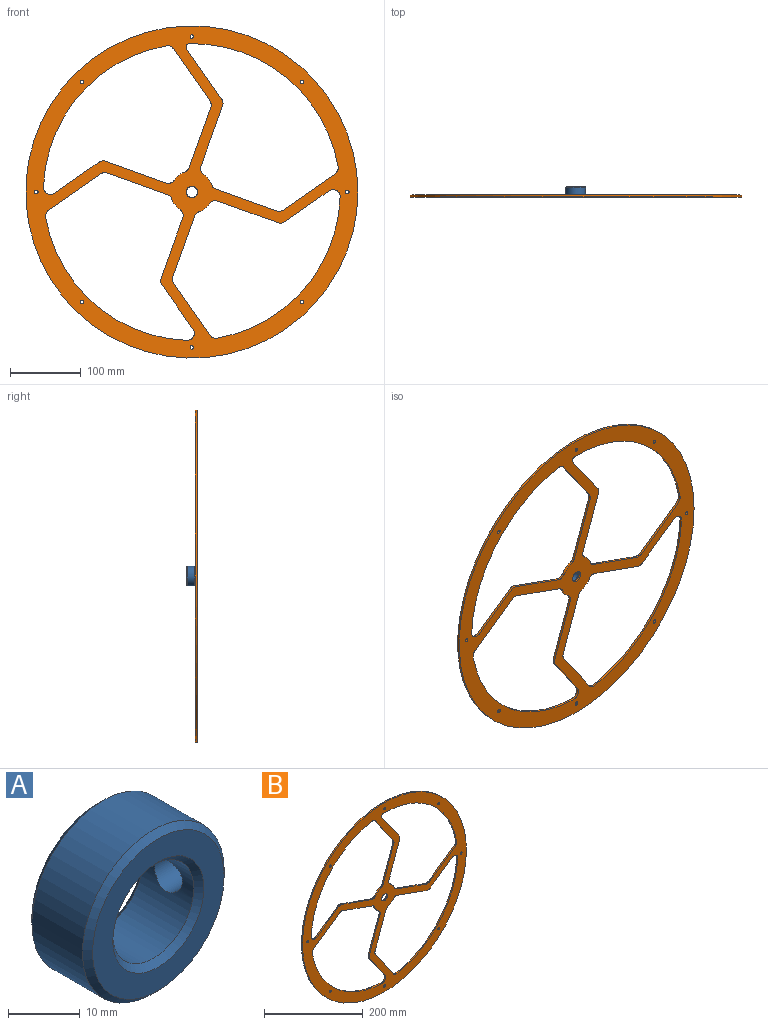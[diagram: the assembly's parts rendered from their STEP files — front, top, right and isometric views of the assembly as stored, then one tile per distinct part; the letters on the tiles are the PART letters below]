
ASSEMBLY  parts=2 mates=1
PART A: 9 faces, bbox 28x12x28 mm
  f0: cylinder r=8mm len=16mm, axis (0,1,0), area 478.6mm2, adj f4,f5,f8
  f1: cylinder r=14mm len=28mm, axis (0,1,0), area 855.9mm2, adj f6,f7,f8
  f2: plane 26x26mm, normal (0,-1,0), area 276.5mm2, adj f4,f6
  f3: plane 26x26mm, normal (0,1,0), area 276.5mm2, adj f5,f7
  f4: cone r=8mm half-angle=45deg, axis (0,-1,0), area 75.5mm2, adj f0,f2
  f5: cone r=9mm half-angle=45deg, axis (0,1,0), area 75.5mm2, adj f0,f3
  f6: cone r=13mm half-angle=45deg, axis (0,1,0), area 120mm2, adj f1,f2
  f7: cone r=14mm half-angle=45deg, axis (0,-1,0), area 120mm2, adj f1,f3
  f8: cylinder r=2.75mm len=6.49mm, axis (1,0,0), area 105.5mm2, adj f0,f1
PART B: 60 faces, bbox 470x3x470 mm
  f0: cylinder r=10mm len=9.9mm, axis (0,1,0), area 34mm2, adj f1,f44,f58,f59
  f1: plane 73.72x51.62mm, normal (0.82,0,0.57), area 270mm2, adj f0,f2,f58,f59
  f2: cylinder r=10mm len=9.11mm, axis (0,1,0), area 28.7mm2, adj f1,f3,f58,f59
  f3: plane 85.6x30.7mm, normal (0.94,0,-0.34), area 272.8mm2, adj f2,f4,f58,f59
  f4: cylinder r=10mm len=6.09mm, axis (0,1,0), area 26.6mm2, adj f3,f5,f58,f59
  f5: cylinder r=30mm len=14.95mm, axis (0,1,0), area 57.7mm2, adj f4,f6,f58,f59
  f6: cylinder r=10mm len=11.68mm, axis (0,1,0), area 39.7mm2, adj f5,f7,f58,f59
  f7: plane 85.6x30.7mm, normal (-0.34,0,-0.94), area 272.8mm2, adj f6,f8,f58,f59
  f8: cylinder r=10mm len=9.11mm, axis (0,1,0), area 28.7mm2, adj f7,f9,f58,f59
  f9: plane 62.85x44.01mm, normal (0.57,0,-0.82), area 230.2mm2, adj f8,f10,f58,f59
  f10: cylinder r=10mm len=15.74mm, axis (0,1,0), area 66.4mm2, adj f9,f44,f58,f59
  f11: cylinder r=10mm len=6.09mm, axis (0,1,0), area 26.6mm2, adj f12,f45,f58,f59
  f12: cylinder r=30mm len=14.95mm, axis (0,1,0), area 57.7mm2, adj f11,f13,f58,f59
  f13: cylinder r=10mm len=11.68mm, axis (0,1,0), area 39.7mm2, adj f12,f14,f58,f59
  f14: plane 85.6x30.7mm, normal (0.94,0,-0.34), area 272.8mm2, adj f13,f15,f58,f59
  f15: cylinder r=10mm len=9.11mm, axis (0,1,0), area 28.7mm2, adj f14,f16,f58,f59
  f16: plane 70.8x49.57mm, normal (0.82,0,0.57), area 259.3mm2, adj f15,f17,f58,f59
  f17: cylinder r=5mm len=7.87mm, axis (0,1,0), area 32.5mm2, adj f16,f18,f58,f59
  f18: cylinder r=210mm len=210.12mm, axis (0,1,0), area 890.9mm2, adj f17,f19,f58,f59
  f19: cylinder r=10mm len=9.9mm, axis (0,1,0), area 34mm2, adj f18,f20,f58,f59
  f20: plane 73.72x51.62mm, normal (-0.57,0,0.82), area 270mm2, adj f19,f21,f58,f59
  f21: cylinder r=10mm len=9.11mm, axis (0,1,0), area 28.7mm2, adj f20,f45,f58,f59
  f22: cylinder r=10mm len=9.11mm, axis (0,1,0), area 28.7mm2, adj f23,f46,f58,f59
  f23: plane 62.85x44.01mm, normal (-0.57,0,0.82), area 230.2mm2, adj f22,f24,f58,f59
  f24: cylinder r=10mm len=15.74mm, axis (0,1,0), area 66.4mm2, adj f23,f25,f58,f59
  f25: cylinder r=210mm len=200.05mm, axis (0,1,0), area 860.7mm2, adj f24,f26,f58,f59
  f26: cylinder r=10mm len=9.9mm, axis (0,1,0), area 34mm2, adj f25,f27,f58,f59
  f27: plane 73.72x51.62mm, normal (-0.82,0,-0.57), area 270mm2, adj f26,f28,f58,f59
  f28: cylinder r=10mm len=9.11mm, axis (0,1,0), area 28.7mm2, adj f27,f29,f58,f59
  f29: plane 85.6x30.7mm, normal (-0.94,0,0.34), area 272.8mm2, adj f28,f30,f58,f59
  f30: cylinder r=10mm len=6.09mm, axis (0,1,0), area 26.6mm2, adj f29,f31,f58,f59
  f31: cylinder r=30mm len=14.95mm, axis (0,1,0), area 57.7mm2, adj f30,f32,f58,f59
  f32: cylinder r=10mm len=11.68mm, axis (0,1,0), area 39.7mm2, adj f31,f46,f58,f59
  f33: cylinder r=10mm len=11.68mm, axis (0,1,0), area 39.7mm2, adj f34,f47,f58,f59
  f34: plane 85.6x30.7mm, normal (-0.94,0,0.34), area 272.8mm2, adj f33,f35,f58,f59
  f35: cylinder r=10mm len=9.11mm, axis (0,1,0), area 28.7mm2, adj f34,f36,f58,f59
  f36: plane 62.85x44.01mm, normal (-0.82,0,-0.57), area 230.2mm2, adj f35,f37,f58,f59
  f37: cylinder r=10mm len=15.74mm, axis (0,1,0), area 66.4mm2, adj f36,f38,f58,f59
  f38: cylinder r=210mm len=200.05mm, axis (0,1,0), area 860.7mm2, adj f37,f39,f58,f59
  f39: cylinder r=10mm len=9.9mm, axis (0,1,0), area 34mm2, adj f38,f40,f58,f59
  f40: plane 73.72x51.62mm, normal (0.57,0,-0.82), area 270mm2, adj f39,f41,f58,f59
  f41: cylinder r=10mm len=9.11mm, axis (0,1,0), area 28.7mm2, adj f40,f42,f58,f59
  f42: plane 85.6x30.7mm, normal (-0.34,0,-0.94), area 272.8mm2, adj f41,f43,f58,f59
  f43: cylinder r=10mm len=6.09mm, axis (0,1,0), area 26.6mm2, adj f42,f47,f58,f59
  f44: cylinder r=210mm len=200.05mm, axis (0,1,0), area 860.7mm2, adj f0,f10,f58,f59
  f45: plane 85.6x30.7mm, normal (0.34,0,0.94), area 272.8mm2, adj f11,f21,f58,f59
  f46: plane 85.6x30.7mm, normal (0.34,0,0.94), area 272.8mm2, adj f22,f32,f58,f59
  f47: cylinder r=30mm len=14.95mm, axis (0,1,0), area 57.7mm2, adj f33,f43,f58,f59
  f48: cylinder r=2.5mm len=5mm, axis (0,1,0), area 47.1mm2, adj f58,f59
  f49: cylinder r=2.5mm len=5mm, axis (0,1,0), area 47.1mm2, adj f58,f59
  f50: cylinder r=2.5mm len=5mm, axis (0,1,0), area 47.1mm2, adj f58,f59
  f51: cylinder r=2.5mm len=5mm, axis (0,1,0), area 47.1mm2, adj f58,f59
  f52: cylinder r=8mm len=16mm, axis (0,1,0), area 150.8mm2, adj f58,f59
  f53: cylinder r=2.5mm len=5mm, axis (0,1,0), area 47.1mm2, adj f58,f59
  f54: cylinder r=2.5mm len=5mm, axis (0,1,0), area 47.1mm2, adj f58,f59
  f55: cylinder r=2.5mm len=5mm, axis (0,1,0), area 47.1mm2, adj f58,f59
  f56: cylinder r=2.5mm len=5mm, axis (0,1,0), area 47.1mm2, adj f58,f59
  f57: cylinder r=235mm len=470mm, axis (0,1,0), area 4429.6mm2, adj f58,f59
  f58: plane 470x470mm, normal (0,-1,0), area 50005.3mm2, adj f0,f1,f2,f3,f4,f5,f6,f7
  f59: plane 470x470mm, normal (0,1,0), area 50005.3mm2, adj f0,f1,f2,f3,f4,f5,f6,f7
PLACE A at identity
PLACE B t=(0,-12,0)mm fixed
MATE fastened B.f5 <-> A.f0  axis (0,1,0) through (0,-12,0)mm
